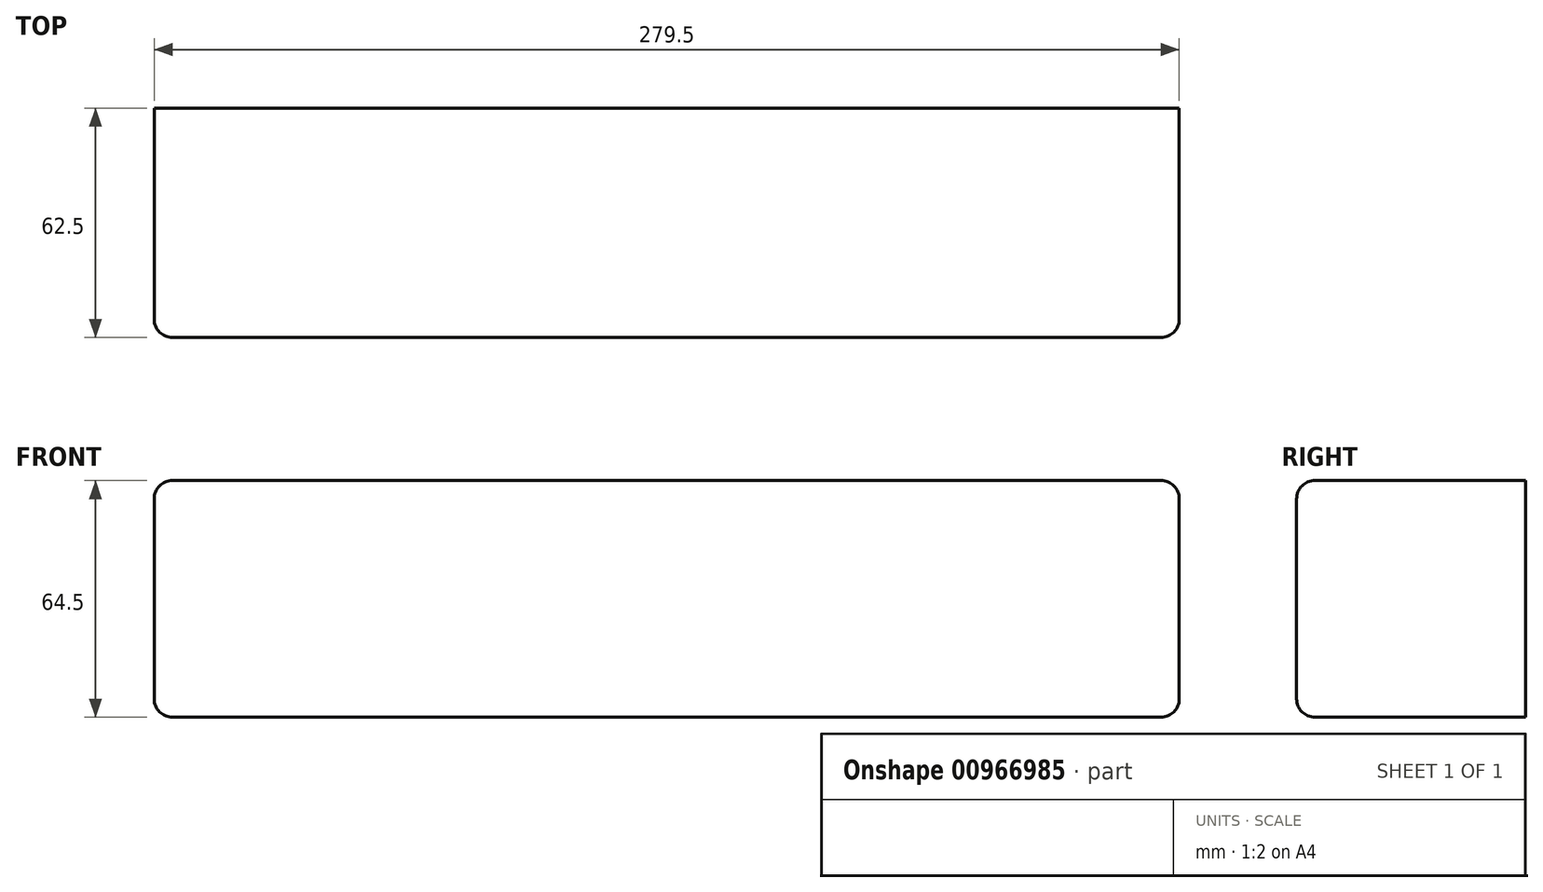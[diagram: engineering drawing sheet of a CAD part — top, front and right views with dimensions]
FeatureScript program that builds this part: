
annotation { "Feature Type Name" : "Feature", "Feature Type Description" : "" }
export const myFeature = defineFeature(function(context is Context, id is Id, definition is map)
    precondition{}
    {
        {
            var Q0;
            Q0=qCreatedBy(makeId("Front.planeOp"),FACE);
            var sketch = newSketch(context, id + "F0", { "sketchPlane" : qUnion([Q0])});
            skLineSegment(sketch, "E0.bottom", {"start": v(0, 0) * mm, "end": v(279.5, 0) * mm});
            skLineSegment(sketch, "E0.top", {"start": v(0, 64.5) * mm, "end": v(279.5, 64.5) * mm});
            skLineSegment(sketch, "E0.left", {"start": v(0, 0) * mm, "end": v(0, 64.5) * mm});
            skLineSegment(sketch, "E0.right", {"start": v(279.5, 0) * mm, "end": v(279.5, 64.5) * mm});
            skSolve(sketch);
        }
        {
            var Q0;
            Q0 = qSketchRegion(id + "F0", true);
            extrude(context, id + "F1", {"entities" : qUnion([Q0]), "depth" : 62.5 * mm, "offsetDistance" : 25 * mm});
        }
        {
            var Q0;
            Q0=makeQuery(id+"F1.opExtrude","CAP_EDGE",EDGE,{"disambiguationData":[OSD([sQuery(id+"F0.wireOp",EDGE,"E0.top")])],"isStart":false});
            var Q1;
            Q1=makeQuery(id+"F1.opExtrude","CAP_EDGE",EDGE,{"disambiguationData":[OSD([sQuery(id+"F0.wireOp",EDGE,"E0.right")])],"isStart":false});
            var Q2;
            Q2=makeQuery(id+"F1.opExtrude","CAP_EDGE",EDGE,{"disambiguationData":[OSD([sQuery(id+"F0.wireOp",EDGE,"E0.bottom")])],"isStart":false});
            var Q3;
            Q3=makeQuery(id+"F1.opExtrude","CAP_EDGE",EDGE,{"disambiguationData":[OSD([sQuery(id+"F0.wireOp",EDGE,"E0.left")])],"isStart":false});
            var Q4;
            Q4=makeQuery(id+"F1.opExtrude","SWEPT_EDGE",EDGE,{"disambiguationData":[OSD([sQuery(id+"F0.wireOp",EDGE,"E0.top"),sQuery(id+"F0.wireOp",EDGE,"E0.left")])]});
            var Q5;
            Q5=makeQuery(id+"F1.opExtrude","SWEPT_EDGE",EDGE,{"disambiguationData":[OSD([sQuery(id+"F0.wireOp",EDGE,"E0.top"),sQuery(id+"F0.wireOp",EDGE,"E0.right")])]});
            var Q6;
            Q6=makeQuery(id+"F1.opExtrude","SWEPT_EDGE",EDGE,{"disambiguationData":[OSD([sQuery(id+"F0.wireOp",EDGE,"E0.bottom"),sQuery(id+"F0.wireOp",EDGE,"E0.right")])]});
            var Q7;
            Q7=makeQuery(id+"F1.opExtrude","SWEPT_EDGE",EDGE,{"disambiguationData":[OSD([sQuery(id+"F0.wireOp",EDGE,"E0.bottom"),sQuery(id+"F0.wireOp",EDGE,"E0.left")])]});
            fillet(context, id + "F2", {"entities" : qUnion([Q0, Q1, Q2, Q3, Q4, Q5, Q6, Q7]), "radius" : 5 * mm, "tangentPropagation" : true, "allowEdgeOverflow" : false});
        }
    });
